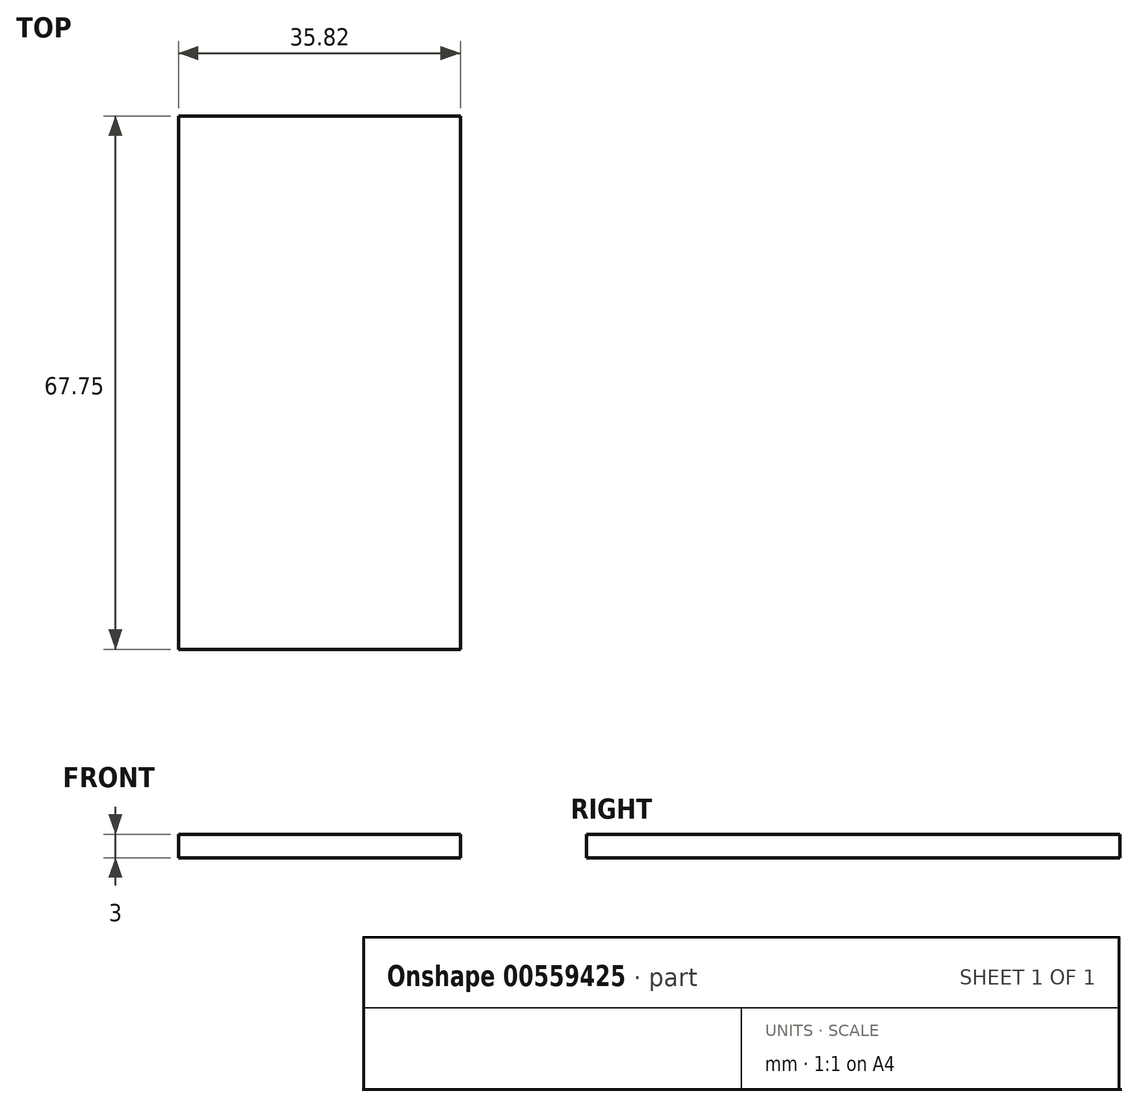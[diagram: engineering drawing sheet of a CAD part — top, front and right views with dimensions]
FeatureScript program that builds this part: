
annotation { "Feature Type Name" : "Feature", "Feature Type Description" : "" }
export const myFeature = defineFeature(function(context is Context, id is Id, definition is map)
    precondition{}
    {
        {
            var Q0;
            Q0=qCreatedBy(makeId("Top.planeOp"),FACE);
            var sketch = newSketch(context, id + "F0", { "sketchPlane" : qUnion([Q0])});
            skLineSegment(sketch, "E0.bottom", {"start": v(0, 0) * mm, "end": v(35.82, 0) * mm});
            skLineSegment(sketch, "E0.top", {"start": v(0, 67.75) * mm, "end": v(35.82, 67.75) * mm});
            skLineSegment(sketch, "E0.left", {"start": v(0, 0) * mm, "end": v(0, 67.75) * mm});
            skLineSegment(sketch, "E0.right", {"start": v(35.82, 0) * mm, "end": v(35.82, 67.75) * mm});
            skSolve(sketch);
        }
        {
            var Q0;
            Q0=makeQuery(id+"F0.imprint","IMPRINT",FACE,{"disambiguationData":[TD([[makeQuery(id+"F0.imprint","IMPRINT",EDGE,{"derivedFrom":sQuery(id+"F0.wireOp",EDGE,"E0.bottom")}),1.0]])]});
            extrude(context, id + "F1", {"entities" : qUnion([Q0]), "depth" : 3 * mm, "offsetDistance" : 25 * mm});
        }
    });
